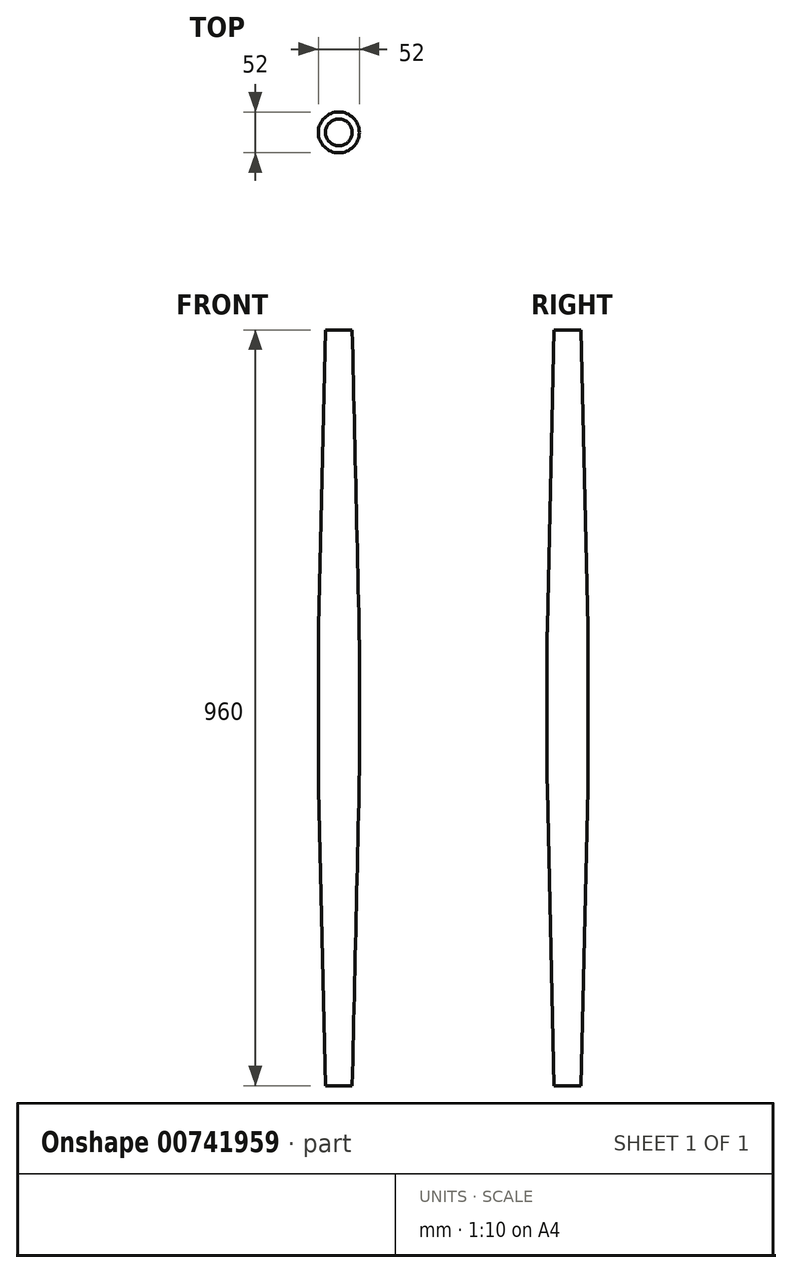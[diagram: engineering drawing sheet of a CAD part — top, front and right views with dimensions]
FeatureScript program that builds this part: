
annotation { "Feature Type Name" : "Feature", "Feature Type Description" : "" }
export const myFeature = defineFeature(function(context is Context, id is Id, definition is map)
    precondition{}
    {
        {
            var Q0;
            Q0=qCreatedBy(makeId("Front.planeOp"),FACE);
            var sketch = newSketch(context, id + "F0", { "sketchPlane" : qUnion([Q0])});
            skLineSegment(sketch, "E0", {"start": v(0, 0) * mm, "end": v(0, 480) * mm});
            skLineSegment(sketch, "E1", {"start": v(0, 480) * mm, "end": v(17, 480) * mm});
            skLineSegment(sketch, "E2", {"start": v(17, 480) * mm, "end": v(25.73, 102.96) * mm});
            skLineSegment(sketch, "E3", {"start": v(26, 79.81) * mm, "end": v(26, 0) * mm});
            skPoint(sketch, "E4.visualSharp", {"position": v(26, 91.39) * mm});
            skArc(sketch, "E4.filletArc", {"start": v(26, 79.81) * mm, "mid": v(25.93, 91.39) * mm, "end": v(25.73, 102.96) * mm});
            skLineSegment(sketch, "E5.MirrorCS", {"start": v(26, -79.81) * mm, "end": v(26, 0) * mm});
            skArc(sketch, "E6.MirrorCS", {"start": v(26, -79.81) * mm, "mid": v(25.93, -91.39) * mm, "end": v(25.73, -102.96) * mm});
            skLineSegment(sketch, "E7.MirrorCS", {"start": v(17, -480) * mm, "end": v(25.73, -102.96) * mm});
            skLineSegment(sketch, "E8.MirrorCS", {"start": v(0, -480) * mm, "end": v(17, -480) * mm});
            skLineSegment(sketch, "E9.MirrorCS", {"start": v(0, 0) * mm, "end": v(0, -480) * mm});
            skSolve(sketch);
        }
        {
            var Q0;
            Q0=makeQuery(id+"F0.imprint","IMPRINT",FACE,{"disambiguationData":[TD([[makeQuery(id+"F0.imprint","IMPRINT",EDGE,{"derivedFrom":sQuery(id+"F0.wireOp",EDGE,"E0")}),-1.0]])]});
            var Q1;
            Q1=makeQuery(id+"F0.imprint","IMPRINT",FACE,{"disambiguationData":[TD([[makeQuery(id+"F0.imprint","IMPRINT",EDGE,{"derivedFrom":sQuery(id+"F0.wireOp",EDGE,"CjWrrxx0-ISEx-yxa1-8jfl-dFYM9Hkqyzem")}),1.0]])]});
            var Q2;
            Q2=sQuery(id+"F0.wireOp",EDGE,"E0");
            revolve(context, id + "F1", {"surfaceOperationType" : NewSurfaceOperationType.NEW, "entities" : qUnion([Q0, Q1]), "axis" : qUnion([Q2]), "revolveType" : RevolveType.FULL, "oppositeDirection" : true});
        }
    });
